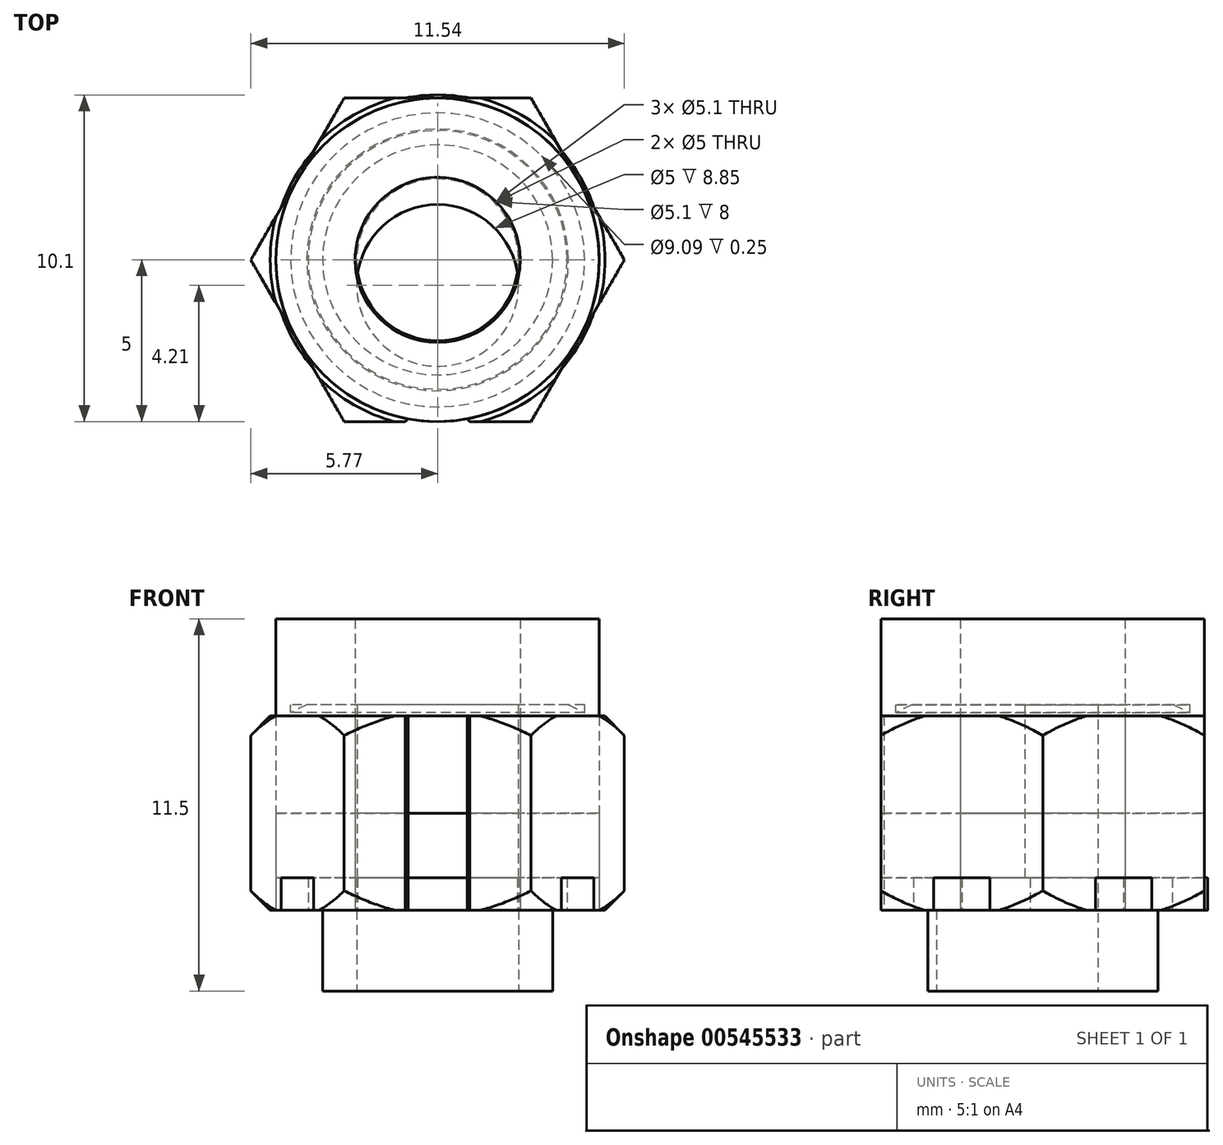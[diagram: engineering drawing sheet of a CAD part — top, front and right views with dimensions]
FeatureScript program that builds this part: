
annotation { "Feature Type Name" : "Feature", "Feature Type Description" : "" }
export const myFeature = defineFeature(function(context is Context, id is Id, definition is map)
    precondition{}
    {
        {
            var Q0;
            Q0=qCreatedBy(makeId("Top.planeOp"),FACE);
            var sketch = newSketch(context, id + "F0", { "sketchPlane" : qUnion([Q0])});
            skArc(sketch, "E0", {"start": v(1.94, -4.72) * mm, "mid": v(0, 5.1) * mm, "end": v(-1.94, -4.72) * mm});
            skCircle(sketch, "E1", {"center": v(0, 0) * mm, "radius": 3.56 * mm});
            skCircle(sketch, "E2", {"center": v(0, -0.79) * mm, "radius": 2.5 * mm});
            skLineSegment(sketch, "E3", {"start": v(-1.94, -4.72) * mm, "end": v(1.94, -4.72) * mm, "construction": true});
            skLineSegment(sketch, "E4", {"start": v(1.94, -4.72) * mm, "end": v(0, -4.22) * mm});
            skLineSegment(sketch, "E5", {"start": v(0, -4.22) * mm, "end": v(-1.94, -4.72) * mm});
            skCircle(sketch, "E6.cCircle", {"center": v(0, 0) * mm, "radius": 3.94 * mm, "construction": true});
            skLineSegment(sketch, "E6.0", {"start": v(-2.27, 3.94) * mm, "end": v(2.27, 3.94) * mm});
            skLineSegment(sketch, "E6.1", {"start": v(2.27, 3.93) * mm, "end": v(4.54, 0) * mm});
            skLineSegment(sketch, "E6.2", {"start": v(4.54, 0) * mm, "end": v(2.27, -3.94) * mm});
            skLineSegment(sketch, "E6.3", {"start": v(2.27, -3.94) * mm, "end": v(-2.27, -3.94) * mm});
            skLineSegment(sketch, "E6.4", {"start": v(-2.27, -3.94) * mm, "end": v(-4.54, 0) * mm});
            skLineSegment(sketch, "E6.5", {"start": v(-4.54, 0) * mm, "end": v(-2.27, 3.94) * mm});
            skPoint(sketch, "E6.0.midPoint", {"position": v(0, 3.94) * mm});
            skSolve(sketch);
        }
        {
            var Q0;
            Q0=makeQuery(id+"F0.imprint","IMPRINT",FACE,{"disambiguationData":[TD([[makeQuery(id+"F0.imprint","IMPRINT",EDGE,{"derivedFrom":sQuery(id+"F0.wireOp",EDGE,"E1")}),-1.0]])]});
            var Q1;
            Q1=makeQuery(id+"F0.imprint","IMPRINT",FACE,{"disambiguationData":[TD([[makeQuery(id+"F0.imprint","IMPRINT",EDGE,{"derivedFrom":sQuery(id+"F0.wireOp",EDGE,"E1")}),1.0]])]});
            extrude(context, id + "F1", {"entities" : qUnion([Q0, Q1]), "depth" : 6.35 * mm, "offsetDistance" : 25 * mm});
        }
        {
            var Q0;
            Q0=makeQuery(id+"F0.imprint","IMPRINT",FACE,{"disambiguationData":[TD([[makeQuery(id+"F0.imprint","IMPRINT",EDGE,{"derivedFrom":sQuery(id+"F0.wireOp",EDGE,"E0")}),1.0]])]});
            extrude(context, id + "F2", {"entities" : qUnion([Q0]), "operationType" : NewBodyOperationType.ADD, "depth" : 1 * mm, "offsetDistance" : 25 * mm});
        }
        {
            var Q0;
            Q0=makeQuery(id+"F0.imprint","IMPRINT",FACE,{"disambiguationData":[TD([[makeQuery(id+"F0.imprint","IMPRINT",EDGE,{"derivedFrom":sQuery(id+"F0.wireOp",EDGE,"E1")}),1.0]])]});
            extrude(context, id + "F3", {"entities" : qUnion([Q0]), "operationType" : NewBodyOperationType.ADD, "oppositeDirection" : true, "depth" : 2.5 * mm, "offsetDistance" : 25 * mm});
        }
        {
            var Q0;
            Q0=qCreatedBy(makeId("Front.planeOp"),FACE);
            var sketch = newSketch(context, id + "F4", { "sketchPlane" : qUnion([Q0])});
            skPoint(sketch, "E7.0", {"position": v(4.54, 6.35) * mm});
            skLineSegment(sketch, "E8", {"start": v(4.54, 6.35) * mm, "end": v(4.54, 6.1) * mm});
            skLineSegment(sketch, "E9", {"start": v(4.54, 6.1) * mm, "end": v(4.04, 6.35) * mm});
            skLineSegment(sketch, "E10", {"start": v(4.04, 6.35) * mm, "end": v(4.54, 6.35) * mm});
            skLineSegment(sketch, "E11", {"start": v(0, 0) * mm, "end": v(0, 6.35) * mm, "construction": true});
            skSolve(sketch);
        }
        {
            var Q0;
            Q0 = qSketchRegion(id + "F4", true);
            var Q1;
            Q1=sQuery(id+"F4.wireOp",EDGE,"E11");
            revolve(context, id + "F5", {"operationType" : NewBodyOperationType.REMOVE, "entities" : qUnion([Q0]), "axis" : qUnion([Q1]), "revolveType" : RevolveType.FULL, "oppositeDirection" : true});
        }
        {
            var Q0;
            Q0=qCreatedBy(makeId("Top.planeOp"),FACE);
            var sketch = newSketch(context, id + "F6", { "sketchPlane" : qUnion([Q0])});
            skCircle(sketch, "E12", {"center": v(0, 0) * mm, "radius": 3.56 * mm});
            skCircle(sketch, "E13", {"center": v(0, -0.79) * mm, "radius": 2.5 * mm});
            skCircle(sketch, "E14.cCircle", {"center": v(0, 0) * mm, "radius": 5 * mm, "construction": true});
            skLineSegment(sketch, "E14.0", {"start": v(-2.89, 5) * mm, "end": v(2.89, 5) * mm});
            skLineSegment(sketch, "E14.1", {"start": v(2.89, 5) * mm, "end": v(5.77, 0) * mm});
            skLineSegment(sketch, "E14.2", {"start": v(5.77, 0) * mm, "end": v(2.89, -5) * mm});
            skLineSegment(sketch, "E14.3", {"start": v(2.89, -5) * mm, "end": v(-2.89, -5) * mm});
            skLineSegment(sketch, "E14.4", {"start": v(-2.89, -5) * mm, "end": v(-5.77, 0) * mm});
            skLineSegment(sketch, "E14.5", {"start": v(-5.77, 0) * mm, "end": v(-2.89, 5) * mm});
            skPoint(sketch, "E14.0.midPoint", {"position": v(0, 5) * mm});
            skLineSegment(sketch, "E15", {"start": v(0, -4) * mm, "end": v(-1, -5) * mm});
            skLineSegment(sketch, "E16", {"start": v(1, -5) * mm, "end": v(0, -4) * mm});
            skLineSegment(sketch, "E17", {"start": v(0, 0) * mm, "end": v(0, 1.8) * mm, "construction": true});
            skSolve(sketch);
        }
        {
            var Q0;
            Q0=makeQuery(id+"F6.imprint","IMPRINT",FACE,{"disambiguationData":[TD([[makeQuery(id+"F6.imprint","IMPRINT",EDGE,{"derivedFrom":sQuery(id+"F6.wireOp",EDGE,"E12")}),1.0]])]});
            extrude(context, id + "F7", {"entities" : qUnion([Q0]), "oppositeDirection" : true, "depth" : 2.5 * mm, "offsetDistance" : 25 * mm});
        }
        {
            var Q0;
            Q0=makeQuery(id+"F6.imprint","IMPRINT",FACE,{"disambiguationData":[TD([[makeQuery(id+"F6.imprint","IMPRINT",EDGE,{"derivedFrom":sQuery(id+"F6.wireOp",EDGE,"E12")}),1.0]])]});
            var Q1;
            Q1=makeQuery(id+"F6.imprint","IMPRINT",FACE,{"disambiguationData":[TD([[makeQuery(id+"F6.imprint","IMPRINT",EDGE,{"derivedFrom":sQuery(id+"F6.wireOp",EDGE,"E12")}),-1.0]])]});
            extrude(context, id + "F8", {"entities" : qUnion([Q0, Q1]), "operationType" : NewBodyOperationType.ADD, "depth" : 6 * mm, "offsetDistance" : 25 * mm});
        }
        {
            var Q0;
            Q0=qCreatedBy(makeId("Front.planeOp"),FACE);
            var sketch = newSketch(context, id + "F9", { "sketchPlane" : qUnion([Q0])});
            skPoint(sketch, "E18.0", {"position": v(-5.77, 6) * mm});
            skLineSegment(sketch, "E19", {"start": v(-5.77, 6) * mm, "end": v(-5.77, 5.4) * mm});
            skLineSegment(sketch, "E20", {"start": v(-5.77, 6) * mm, "end": v(-5.17, 6) * mm});
            skLineSegment(sketch, "E21", {"start": v(-5.77, 5.4) * mm, "end": v(-5.17, 6) * mm});
            skLineSegment(sketch, "E22", {"start": v(0, 0) * mm, "end": v(0, 2) * mm, "construction": true});
            skPoint(sketch, "E23.0", {"position": v(-5.77, 3) * mm});
            skLineSegment(sketch, "E24", {"start": v(-5.77, 3) * mm, "end": v(-3.77, 3) * mm, "construction": true});
            skLineSegment(sketch, "E25.MirrorCS", {"start": v(-5.77, 0.6) * mm, "end": v(-5.17, 0) * mm});
            skLineSegment(sketch, "E26.MirrorCS", {"start": v(-5.77, 0) * mm, "end": v(-5.17, 0) * mm});
            skLineSegment(sketch, "E27.MirrorCS", {"start": v(-5.77, 0) * mm, "end": v(-5.77, 0.6) * mm});
            skPoint(sketch, "E28.MirrorP", {"position": v(-5.77, 0) * mm});
            skSolve(sketch);
        }
        {
            var Q0;
            Q0=makeQuery(id+"F9.imprint","IMPRINT",FACE,{"disambiguationData":[TD([[makeQuery(id+"F9.imprint","IMPRINT",EDGE,{"derivedFrom":sQuery(id+"F9.wireOp",EDGE,"E19")}),1.0]])]});
            var Q1;
            Q1=makeQuery(id+"F9.imprint","IMPRINT",FACE,{"disambiguationData":[TD([[makeQuery(id+"F9.imprint","IMPRINT",EDGE,{"derivedFrom":sQuery(id+"F9.wireOp",EDGE,"E25.MirrorCS")}),-1.0]])]});
            var Q2;
            Q2=sQuery(id+"F9.wireOp",EDGE,"E22");
            revolve(context, id + "F10", {"operationType" : NewBodyOperationType.REMOVE, "entities" : qUnion([Q0, Q1]), "axis" : qUnion([Q2]), "revolveType" : RevolveType.FULL, "oppositeDirection" : true});
        }
        {
            var Q0;
            Q0=qCreatedBy(makeId("Top.planeOp"),FACE);
            var sketch = newSketch(context, id + "F11", { "sketchPlane" : qUnion([Q0])});
            skCircle(sketch, "E29", {"center": v(0, 0) * mm, "radius": 2.5 * mm});
            skCircle(sketch, "E30", {"center": v(0, 0) * mm, "radius": 5 * mm});
            skCircle(sketch, "E31", {"center": v(0, 0) * mm, "radius": 4 * mm});
            skSolve(sketch);
        }
        {
            var Q0;
            Q0 = qSketchRegion(id + "F11", true);
            var Q1;
            Q1=makeQuery(id+"F11.imprint","IMPRINT",FACE,{"disambiguationData":[TD([[makeQuery(id+"F11.imprint","IMPRINT",EDGE,{"derivedFrom":sQuery(id+"F11.wireOp",EDGE,"E29")}),-1.0]])]});
            extrude(context, id + "F12", {"entities" : qUnion([Q0, Q1]), "depth" : 1 * mm, "offsetDistance" : 25 * mm});
        }
        {
            var Q0;
            Q0=makeQuery(id+"F11.imprint","IMPRINT",FACE,{"disambiguationData":[TD([[makeQuery(id+"F11.imprint","IMPRINT",EDGE,{"derivedFrom":sQuery(id+"F11.wireOp",EDGE,"E29")}),-1.0]])]});
            extrude(context, id + "F13", {"entities" : qUnion([Q0]), "depth" : 1 * mm, "offsetDistance" : 25 * mm});
        }
        {
            var Q0;
            Q0=qCreatedBy(makeId("Top.planeOp"),FACE);
            var sketch = newSketch(context, id + "F14", { "sketchPlane" : qUnion([Q0])});
            skCircle(sketch, "E32", {"center": v(0, 0) * mm, "radius": 5 * mm});
            skCircle(sketch, "E33", {"center": v(0, 0) * mm, "radius": 2.55 * mm});
            skSolve(sketch);
        }
        {
            var Q0;
            Q0=makeQuery(id+"F14.imprint","IMPRINT",FACE,{"disambiguationData":[TD([[makeQuery(id+"F14.imprint","IMPRINT",EDGE,{"derivedFrom":sQuery(id+"F14.wireOp",EDGE,"E32")}),1.0]])]});
            extrude(context, id + "F15", {"entities" : qUnion([Q0]), "depth" : 6 * mm, "offsetDistance" : 25 * mm});
        }
        {
            var Q0;
            Q0=makeQuery(id+"F14.imprint","IMPRINT",FACE,{"disambiguationData":[TD([[makeQuery(id+"F14.imprint","IMPRINT",EDGE,{"derivedFrom":sQuery(id+"F14.wireOp",EDGE,"E32")}),1.0]])]});
            extrude(context, id + "F16", {"entities" : qUnion([Q0]), "depth" : 3 * mm, "offsetDistance" : 25 * mm});
        }
        {
            var Q0;
            Q0=makeQuery(id+"F14.imprint","IMPRINT",FACE,{"disambiguationData":[TD([[makeQuery(id+"F14.imprint","IMPRINT",EDGE,{"derivedFrom":sQuery(id+"F14.wireOp",EDGE,"E32")}),1.0]])]});
            extrude(context, id + "F17", {"entities" : qUnion([Q0]), "depth" : 9 * mm, "offsetDistance" : 25 * mm});
        }
    });
